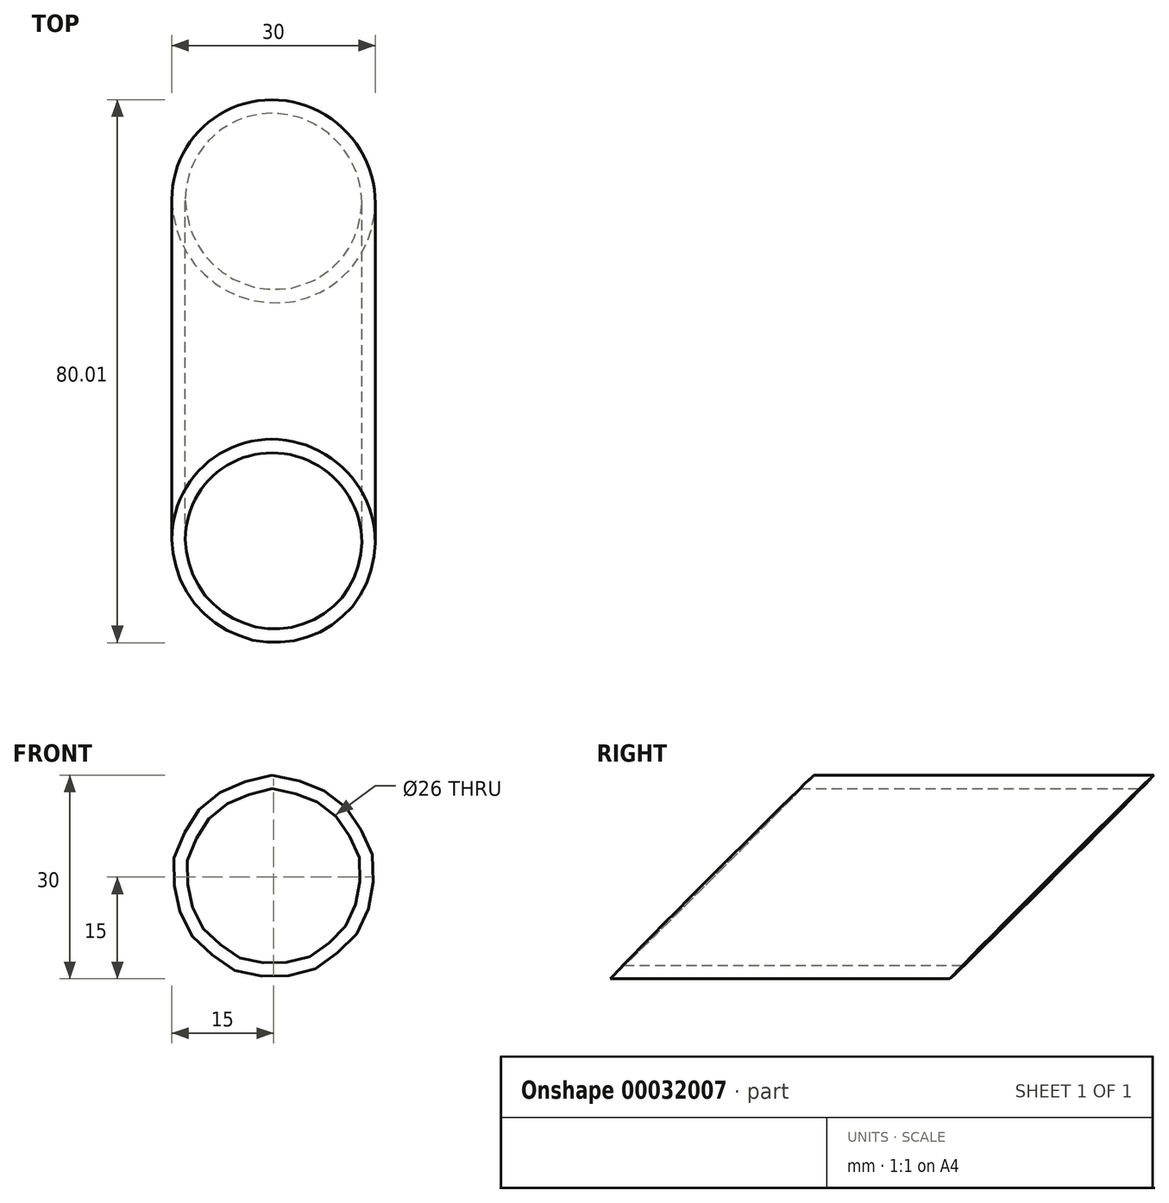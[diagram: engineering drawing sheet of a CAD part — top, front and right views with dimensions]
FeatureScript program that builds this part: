
annotation { "Feature Type Name" : "Feature", "Feature Type Description" : "" }
export const myFeature = defineFeature(function(context is Context, id is Id, definition is map)
    precondition{}
    {
        {
            var Q0;
            Q0=qCreatedBy(makeId("Front.planeOp"),FACE);
            var sketch = newSketch(context, id + "F0", { "sketchPlane" : qUnion([Q0])});
            skCircle(sketch, "E0", {"center": v(0, 0) * mm, "radius": 13 * mm});
            skCircle(sketch, "E1", {"center": v(0, 0) * mm, "radius": 15 * mm});
            skSolve(sketch);
        }
        {
            var Q0;
            Q0 = qSketchRegion(id + "F0", true);
            extrude(context, id + "F1", {"entities" : qUnion([Q0]), "depth" : 100 * mm});
        }
        {
            var Q0;
            Q0=qCreatedBy(makeId("Front.planeOp"),FACE);
            var sketch = newSketch(context, id + "F2", { "sketchPlane" : qUnion([Q0])});
            skLineSegment(sketch, "E2", {"start": v(70, 0) * mm, "end": v(-68.29, -2.3) * mm});
            skSolve(sketch);
        }
        {
            var Q0;
            Q0=sQuery(id+"F2.wireOp",EDGE,"E2");
            cPlane(context, id + "F3", {"entities" : qUnion([Q0]), "cplaneType" : CPlaneType.LINE_ANGLE, "offset" : 150 * mm, "angle" : 45 * degree, "width" : 150 * mm, "height" : 150 * mm});
        }
        {
            var Q0;
            Q0=qCreatedBy(id+"F3.planeOp",FACE);
            cPlane(context, id + "F4", {"entities" : qUnion([Q0]), "cplaneType" : CPlaneType.OFFSET, "offset" : 15 * mm, "width" : 150 * mm, "height" : 150 * mm});
        }
        {
            var Q0;
            Q0=qCreatedBy(id+"F4.planeOp",FACE);
            var sketch = newSketch(context, id + "F5", { "sketchPlane" : qUnion([Q0])});
            skLineSegment(sketch, "E3.bottom", {"start": v(36.46, 19.27) * mm, "end": v(-41.97, 19.27) * mm});
            skLineSegment(sketch, "E3.top", {"start": v(36.46, -49.07) * mm, "end": v(-41.97, -49.07) * mm});
            skLineSegment(sketch, "E3.left", {"start": v(36.46, 19.27) * mm, "end": v(36.46, -49.07) * mm});
            skLineSegment(sketch, "E3.right", {"start": v(-41.97, 19.27) * mm, "end": v(-41.97, -49.07) * mm});
            skSolve(sketch);
        }
        {
            var Q0;
            Q0 = qSketchRegion(id + "F5", true);
            extrude(context, id + "F6", {"entities" : qUnion([Q0]), "operationType" : NewBodyOperationType.REMOVE, "oppositeDirection" : true, "depth" : 25 * mm});
        }
        {
            var Q0;
            Q0=qCreatedBy(id+"F4.planeOp",FACE);
            cPlane(context, id + "F7", {"entities" : qUnion([Q0]), "cplaneType" : CPlaneType.OFFSET, "offset" : 35.36 * mm, "width" : 150 * mm, "height" : 150 * mm});
        }
        {
            var Q0;
            Q0=qCreatedBy(id+"F7.planeOp",FACE);
            var sketch = newSketch(context, id + "F8", { "sketchPlane" : qUnion([Q0])});
            skLineSegment(sketch, "E4.bottom", {"start": v(-63.8, -22.96) * mm, "end": v(83.68, -22.96) * mm});
            skLineSegment(sketch, "E4.top", {"start": v(-63.8, -91.25) * mm, "end": v(83.68, -91.25) * mm});
            skLineSegment(sketch, "E4.left", {"start": v(-63.8, -22.96) * mm, "end": v(-63.8, -91.25) * mm});
            skLineSegment(sketch, "E4.right", {"start": v(83.68, -22.96) * mm, "end": v(83.68, -91.25) * mm});
            skSolve(sketch);
        }
        {
            var Q0;
            Q0 = qSketchRegion(id + "F8", true);
            extrude(context, id + "F9", {"entities" : qUnion([Q0]), "operationType" : NewBodyOperationType.REMOVE, "depth" : 35 * mm});
        }
    });
